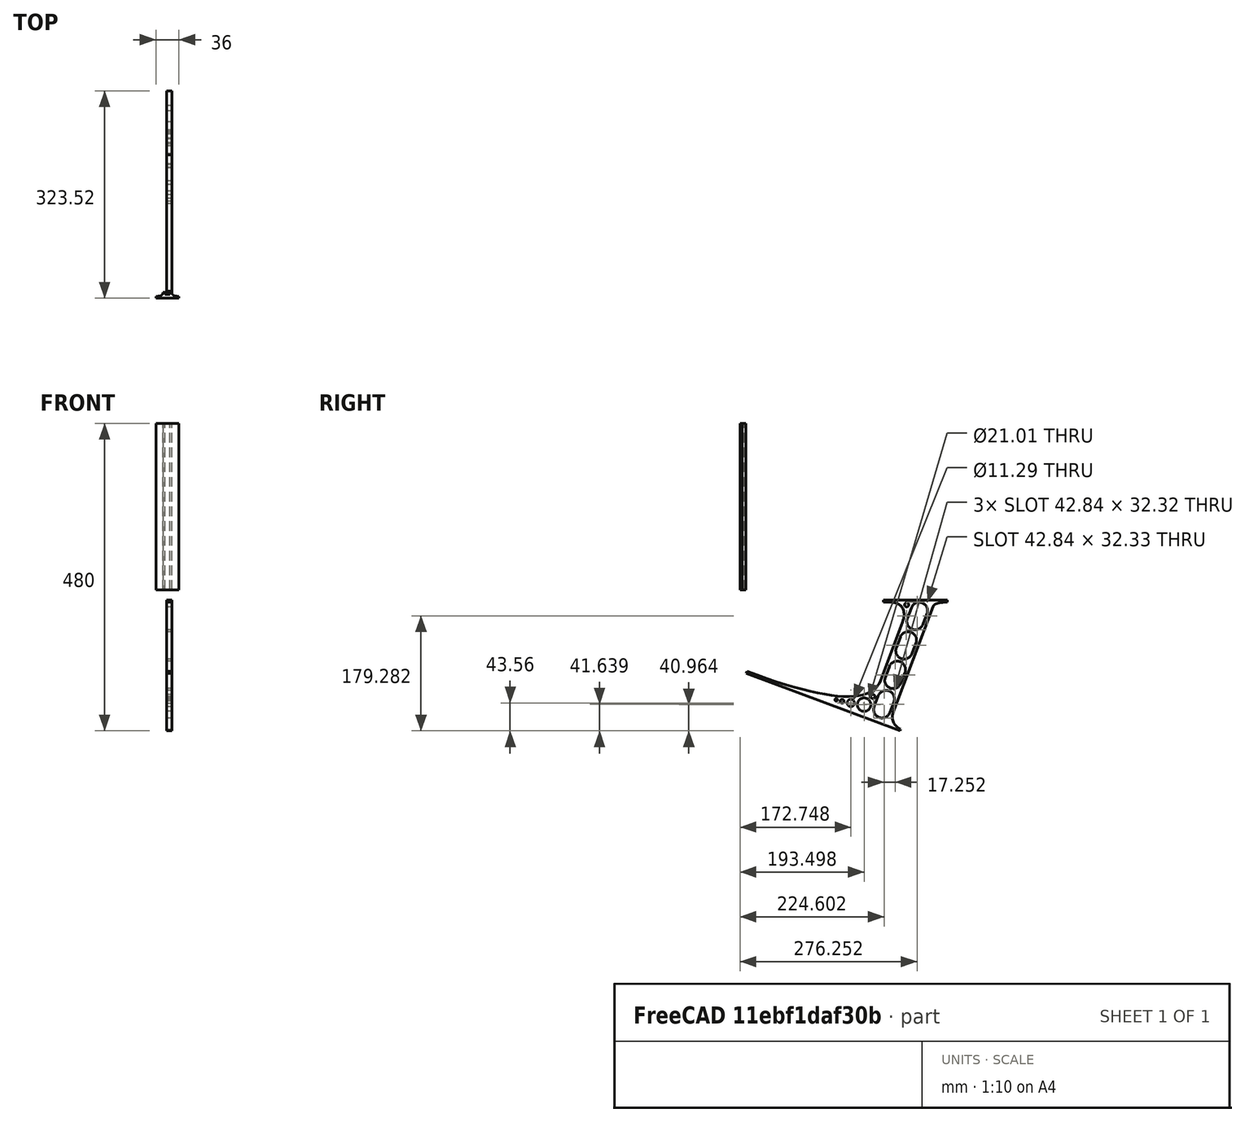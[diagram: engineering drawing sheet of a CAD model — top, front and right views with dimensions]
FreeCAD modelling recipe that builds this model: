
FCSTD DOCUMENT  (FreeCAD 0.19R0.19.2)
Label: laptopStand079
License: All rights reserved
LicenseURL: http://en.wikipedia.org/wiki/All_rights_reserved
objects: Sketcher::SketchObject×3, Part::Extrusion×3
note: 6 computed .brp shape members not serialized (recipe doc carries the construction recipe); baked Part::Feature solids carry a one-line shape summary decoded from their .brp

FEATURE [Sketcher::SketchObject] Sketch
  FullyConstrained = true
  sketch-geometry (204):
    g0: LineSegment StartX=-10.9272 StartY=-82.7794 StartZ=0 EndX=46.0728 EndY=-51.4823 EndZ=0
    g1: LineSegment StartX=366.073 StartY=-91.7794 StartZ=0 EndX=318.073 EndY=-65.424 EndZ=0
    g2: LineSegment StartX=-10.9272 StartY=77.3346 StartZ=0 EndX=-10.9272 EndY=-82.7794 EndZ=0
    g3: LineSegment StartX=375.073 StartY=-82.7794 StartZ=0 EndX=375.073 EndY=83.9235 EndZ=0
    g4: LineSegment StartX=-1.92719 StartY=-91.7794 StartZ=0 EndX=46.0728 EndY=-91.7794 EndZ=0
    g5: LineSegment StartX=318.073 StartY=124.221 StartZ=0 EndX=366.073 EndY=124.221 EndZ=0
    g6: LineSegment StartX=306.073 StartY=124.221 StartZ=0 EndX=189.124 EndY=27.0628 EndZ=0
    g7: LineSegment StartX=58.0728 StartY=-91.7794 StartZ=0 EndX=175.022 EndY=5.37834 EndZ=0
    g8: LineSegment StartX=175.022 StartY=27.0628 StartZ=0 EndX=58.0728 EndY=124.221 EndZ=0
    g9: LineSegment StartX=189.124 StartY=5.37834 StartZ=0 EndX=306.073 EndY=-91.7794 EndZ=0
    g10: LineSegment StartX=306.073 StartY=77.3346 StartZ=0 EndX=306.073 EndY=-44.8935 EndZ=0
    g11: LineSegment StartX=318.073 StartY=83.9235 StartZ=0 EndX=318.073 EndY=-51.4823 EndZ=0
    g12: LineSegment StartX=318.073 StartY=-51.4823 StartZ=0 EndX=375.073 EndY=-82.7794 EndZ=0
    g13: LineSegment StartX=318.073 StartY=-65.424 StartZ=0 EndX=318.073 EndY=-91.7794 EndZ=0
    g14: LineSegment StartX=318.073 StartY=-91.7794 StartZ=0 EndX=366.073 EndY=-91.7794 EndZ=0
    g15: LineSegment StartX=58.0728 StartY=-44.8935 StartZ=0 EndX=58.0728 EndY=77.3346 EndZ=0
    g16: LineSegment StartX=46.0728 StartY=-65.424 StartZ=0 EndX=-1.92719 EndY=-91.7794 EndZ=0
    g17: LineSegment StartX=46.0728 StartY=-65.424 StartZ=0 EndX=46.0728 EndY=-91.7794 EndZ=0
    g18: LineSegment StartX=46.0728 StartY=77.3346 StartZ=0 EndX=46.0728 EndY=-51.4823 EndZ=0
    g19: LineSegment StartX=-42.9272 StartY=136.221 StartZ=0 EndX=-42.9272 EndY=-103.779 EndZ=0
    g20: LineSegment StartX=407.073 StartY=136.221 StartZ=0 EndX=407.073 EndY=-103.779 EndZ=0
    g21: LineSegment StartX=179.022 StartY=27.0628 StartZ=0 EndX=179.022 EndY=124.221 EndZ=0
    g22: LineSegment StartX=185.124 StartY=27.0628 StartZ=0 EndX=185.124 EndY=124.221 EndZ=0
    g23: ArcOfCircle CenterX=-26.9272 CenterY=22.1087 CenterZ=0 NormalX=0 NormalY=0 NormalZ=1 AngleXU=0 Radius=8 StartAngle=1e-16 EndAngle=3.14159
    g24: ArcOfCircle CenterX=-26.9272 CenterY=-83.7794 CenterZ=0 NormalX=0 NormalY=0 NormalZ=1 AngleXU=0 Radius=8 StartAngle=3.14159 EndAngle=6.28319
    g25: LineSegment StartX=-34.9272 StartY=22.1087 StartZ=0 EndX=-34.9272 EndY=-83.7794 EndZ=0
    g26: LineSegment StartX=-18.9272 StartY=22.1087 StartZ=0 EndX=-18.9272 EndY=-83.7794 EndZ=0
    g27: LineSegment StartX=185.124 StartY=-91.7794 StartZ=0 EndX=306.073 EndY=-91.7794 EndZ=0
    g28: LineSegment StartX=179.022 StartY=-91.7794 StartZ=0 EndX=58.0728 EndY=-91.7794 EndZ=0
    g29: LineSegment StartX=306.073 StartY=124.221 StartZ=0 EndX=185.124 EndY=124.221 EndZ=0
    g30: LineSegment StartX=179.022 StartY=124.221 StartZ=0 EndX=58.0728 EndY=124.221 EndZ=0
    g31: ArcOfCircle CenterX=391.073 CenterY=22.1087 CenterZ=0 NormalX=0 NormalY=0 NormalZ=1 AngleXU=0 Radius=8 StartAngle=-4.4e-15 EndAngle=3.14159
    g32: LineSegment StartX=399.073 StartY=22.1087 StartZ=0 EndX=399.073 EndY=-83.7794 EndZ=0
    g33: LineSegment StartX=383.073 StartY=22.1087 StartZ=0 EndX=383.073 EndY=-83.7794 EndZ=0
    g34: ArcOfCircle CenterX=391.073 CenterY=-83.7794 CenterZ=0 NormalX=0 NormalY=0 NormalZ=1 AngleXU=0 Radius=8 StartAngle=3.14159 EndAngle=6.28319
    g35: Circle CenterX=175.022 CenterY=27.0628 CenterZ=0 NormalX=0 NormalY=0 NormalZ=1 AngleXU=0 Radius=1
    g36: Circle CenterX=179.022 CenterY=24.8665 CenterZ=0 NormalX=0 NormalY=0 NormalZ=1 AngleXU=0 Radius=1
    g37: Circle CenterX=179.022 CenterY=27.0628 CenterZ=0 NormalX=0 NormalY=0 NormalZ=1 AngleXU=0 Radius=1
    g38: BSplineCurve PolesCount=3 KnotsCount=2 Degree=2 IsPeriodic=0
    g39: GeomPoint X=175.022 Y=27.0628 Z=0
    g40: GeomPoint X=179.022 Y=27.0628 Z=0
    g41: Circle CenterX=189.124 CenterY=27.0628 CenterZ=0 NormalX=0 NormalY=0 NormalZ=1 AngleXU=0 Radius=1
    g42: Circle CenterX=185.124 CenterY=24.8665 CenterZ=0 NormalX=0 NormalY=0 NormalZ=1 AngleXU=0 Radius=1
    g43: Circle CenterX=185.124 CenterY=27.0628 CenterZ=0 NormalX=0 NormalY=0 NormalZ=1 AngleXU=0 Radius=1
    g44: BSplineCurve PolesCount=3 KnotsCount=2 Degree=2 IsPeriodic=0
    g45: GeomPoint X=189.124 Y=27.0628 Z=0
    g46: GeomPoint X=185.124 Y=27.0628 Z=0
    g47: Circle CenterX=175.022 CenterY=5.37834 CenterZ=0 NormalX=0 NormalY=0 NormalZ=1 AngleXU=0 Radius=1
    g48: Circle CenterX=179.022 CenterY=7.57463 CenterZ=0 NormalX=0 NormalY=0 NormalZ=1 AngleXU=0 Radius=1
    g49: Circle CenterX=179.022 CenterY=5.34704 CenterZ=0 NormalX=0 NormalY=0 NormalZ=1 AngleXU=0 Radius=1
    g50: BSplineCurve PolesCount=3 KnotsCount=2 Degree=2 IsPeriodic=0
    g51: GeomPoint X=175.022 Y=5.37834 Z=0
    g52: GeomPoint X=179.022 Y=5.34704 Z=0
    g53: Circle CenterX=189.124 CenterY=5.37834 CenterZ=0 NormalX=0 NormalY=0 NormalZ=1 AngleXU=0 Radius=1
    g54: Circle CenterX=185.124 CenterY=7.57463 CenterZ=0 NormalX=0 NormalY=0 NormalZ=1 AngleXU=0 Radius=1
    g55: Circle CenterX=185.124 CenterY=5.34704 CenterZ=0 NormalX=0 NormalY=0 NormalZ=1 AngleXU=0 Radius=1
    g56: BSplineCurve PolesCount=3 KnotsCount=2 Degree=2 IsPeriodic=0
    g57: GeomPoint X=189.124 Y=5.37834 Z=0
    g58: GeomPoint X=185.124 Y=5.34704 Z=0
    g59: LineSegment StartX=179.022 StartY=5.34704 StartZ=0 EndX=179.022 EndY=-91.7794 EndZ=0
    g60: LineSegment StartX=185.124 StartY=-91.7794 StartZ=0 EndX=185.124 EndY=5.34704 EndZ=0
    g61: Circle CenterX=165.871 CenterY=18.1458 CenterZ=0 NormalX=0 NormalY=0 NormalZ=1 AngleXU=0 Radius=1
    g62: Circle CenterX=169.377 CenterY=16.2206 CenterZ=0 NormalX=0 NormalY=0 NormalZ=1 AngleXU=0 Radius=1
    g63: Circle CenterX=165.871 CenterY=14.2954 CenterZ=0 NormalX=0 NormalY=0 NormalZ=1 AngleXU=0 Radius=1
    g64: BSplineCurve PolesCount=3 KnotsCount=2 Degree=2 IsPeriodic=0
    g65: GeomPoint X=165.871 Y=18.1458 Z=0
    g66: GeomPoint X=165.871 Y=14.2954 Z=0
    g67: Circle CenterX=198.275 CenterY=18.1458 CenterZ=0 NormalX=0 NormalY=0 NormalZ=1 AngleXU=0 Radius=1
    g68: Circle CenterX=194.768 CenterY=16.2206 CenterZ=0 NormalX=0 NormalY=0 NormalZ=1 AngleXU=0 Radius=1
    g69: Circle CenterX=198.275 CenterY=14.2954 CenterZ=0 NormalX=0 NormalY=0 NormalZ=1 AngleXU=0 Radius=1
    g70: BSplineCurve PolesCount=3 KnotsCount=2 Degree=2 IsPeriodic=0
    g71: GeomPoint X=198.275 Y=18.1458 Z=0
    g72: GeomPoint X=198.275 Y=14.2954 Z=0
    g73: LineSegment StartX=165.871 StartY=18.1458 StartZ=0 EndX=58.0728 EndY=77.3346 EndZ=0
    g74: LineSegment StartX=58.0728 StartY=-44.8935 StartZ=0 EndX=165.871 EndY=14.2954 EndZ=0
    g75: LineSegment StartX=198.275 StartY=18.1458 StartZ=0 EndX=306.073 EndY=77.3346 EndZ=0
    g76: LineSegment StartX=198.275 StartY=14.2954 StartZ=0 EndX=306.073 EndY=-44.8935 EndZ=0
    g77: LineSegment StartX=407.073 StartY=-103.779 StartZ=0 EndX=-42.9272 EndY=-103.779 EndZ=0
    g78: LineSegment StartX=407.073 StartY=136.221 StartZ=0 EndX=-42.9272 EndY=136.221 EndZ=0
    g79: LineSegment StartX=46.0728 StartY=77.3346 StartZ=0 EndX=-10.9272 EndY=77.3346 EndZ=0
    g80: LineSegment StartX=46.0728 StartY=105.865 StartZ=0 EndX=31.5028 EndY=105.865 EndZ=0
    g81: LineSegment StartX=46.0728 StartY=124.221 StartZ=0 EndX=46.0728 EndY=105.865 EndZ=0
    g82: LineSegment StartX=-1.92719 StartY=124.221 StartZ=0 EndX=31.5028 EndY=105.865 EndZ=0
    g83: LineSegment StartX=46.0728 StartY=124.221 StartZ=0 EndX=-1.92719 EndY=124.221 EndZ=0
    g84: LineSegment StartX=318.073 StartY=83.9235 StartZ=0 EndX=375.073 EndY=83.9235 EndZ=0
    g85: LineSegment StartX=318.073 StartY=105.865 StartZ=0 EndX=332.643 EndY=105.865 EndZ=0
    g86: LineSegment StartX=332.643 StartY=105.865 StartZ=0 EndX=366.073 EndY=124.221 EndZ=0
    g87: LineSegment StartX=318.073 StartY=124.221 StartZ=0 EndX=318.073 EndY=105.865 EndZ=0
    g88: Circle CenterX=125.607 CenterY=54.1951 CenterZ=0 NormalX=0 NormalY=0 NormalZ=1 AngleXU=0 Radius=1
    g89: Circle CenterX=139.632 CenterY=46.4944 CenterZ=0 NormalX=0 NormalY=0 NormalZ=1 AngleXU=0 Radius=1
    g90: Circle CenterX=127.326 CenterY=56.7187 CenterZ=0 NormalX=0 NormalY=0 NormalZ=1 AngleXU=0 Radius=1
    g91: BSplineCurve PolesCount=3 KnotsCount=2 Degree=2 IsPeriodic=0
    g92: GeomPoint X=125.607 Y=54.1951 Z=0
    g93: GeomPoint X=127.326 Y=56.7187 Z=0
    g94: Circle CenterX=236.821 CenterY=56.7187 CenterZ=0 NormalX=0 NormalY=0 NormalZ=1 AngleXU=0 Radius=1
    g95: Circle CenterX=224.513 CenterY=46.4944 CenterZ=0 NormalX=0 NormalY=0 NormalZ=1 AngleXU=0 Radius=1
    g96: Circle CenterX=238.538 CenterY=54.1951 CenterZ=0 NormalX=0 NormalY=0 NormalZ=1 AngleXU=0 Radius=1
    g97: BSplineCurve PolesCount=3 KnotsCount=2 Degree=2 IsPeriodic=0
    g98: GeomPoint X=236.821 Y=56.7187 Z=0
    g99: GeomPoint X=238.538 Y=54.1951 Z=0
    g100: Circle CenterX=238.538 CenterY=-21.7539 CenterZ=0 NormalX=0 NormalY=0 NormalZ=1 AngleXU=0 Radius=1
    g101: Circle CenterX=224.513 CenterY=-14.0532 CenterZ=0 NormalX=0 NormalY=0 NormalZ=1 AngleXU=0 Radius=1
    g102: Circle CenterX=236.821 CenterY=-24.2775 CenterZ=0 NormalX=0 NormalY=0 NormalZ=1 AngleXU=0 Radius=1
    g103: BSplineCurve PolesCount=3 KnotsCount=2 Degree=2 IsPeriodic=0
    g104: GeomPoint X=238.538 Y=-21.7539 Z=0
    g105: GeomPoint X=236.821 Y=-24.2775 Z=0
    g106: Circle CenterX=125.607 CenterY=-21.7539 CenterZ=0 NormalX=0 NormalY=0 NormalZ=1 AngleXU=0 Radius=1
    g107: Circle CenterX=139.632 CenterY=-14.0532 CenterZ=0 NormalX=0 NormalY=0 NormalZ=1 AngleXU=0 Radius=1
    g108: Circle CenterX=127.325 CenterY=-24.2775 CenterZ=0 NormalX=0 NormalY=0 NormalZ=1 AngleXU=0 Radius=1
    g109: BSplineCurve PolesCount=3 KnotsCount=2 Degree=2 IsPeriodic=0
    g110: GeomPoint X=125.607 Y=-21.7539 Z=0
    g111: GeomPoint X=127.325 Y=-24.2775 Z=0
    g112: Circle CenterX=302.996 CenterY=111.695 CenterZ=0 NormalX=0 NormalY=0 NormalZ=1 AngleXU=0 Radius=1
    g113: Circle CenterX=306.073 CenterY=114.251 CenterZ=0 NormalX=0 NormalY=0 NormalZ=1 AngleXU=0 Radius=1
    g114: Circle CenterX=306.073 CenterY=110.251 CenterZ=0 NormalX=0 NormalY=0 NormalZ=1 AngleXU=0 Radius=1
    g115: BSplineCurve PolesCount=3 KnotsCount=2 Degree=2 IsPeriodic=0
    g116: GeomPoint X=302.996 Y=111.695 Z=0
    g117: GeomPoint X=306.073 Y=110.251 Z=0
    g118: Circle CenterX=306.073 CenterY=95.2763 CenterZ=0 NormalX=0 NormalY=0 NormalZ=1 AngleXU=0 Radius=1
    g119: Circle CenterX=306.073 CenterY=91.2763 CenterZ=0 NormalX=0 NormalY=0 NormalZ=1 AngleXU=0 Radius=1
    g120: Circle CenterX=302.567 CenterY=89.3511 CenterZ=0 NormalX=0 NormalY=0 NormalZ=1 AngleXU=0 Radius=1
    g121: BSplineCurve PolesCount=3 KnotsCount=2 Degree=2 IsPeriodic=0
    g122: GeomPoint X=306.073 Y=95.2763 Z=0
    g123: GeomPoint X=302.567 Y=89.3511 Z=0
    g124: LineSegment StartX=306.073 StartY=110.251 StartZ=0 EndX=306.073 EndY=95.2763 EndZ=0
    g125: LineSegment StartX=302.996 StartY=111.695 StartZ=0 EndX=236.821 EndY=56.7187 EndZ=0
    g126: LineSegment StartX=238.538 StartY=54.1951 StartZ=0 EndX=302.567 EndY=89.3511 EndZ=0
    g127: Circle CenterX=61.1496 CenterY=111.695 CenterZ=0 NormalX=0 NormalY=0 NormalZ=1 AngleXU=0 Radius=1
    g128: Circle CenterX=58.0728 CenterY=114.251 CenterZ=0 NormalX=0 NormalY=0 NormalZ=1 AngleXU=0 Radius=1
    g129: Circle CenterX=58.0728 CenterY=110.251 CenterZ=0 NormalX=0 NormalY=0 NormalZ=1 AngleXU=0 Radius=1
    g130: BSplineCurve PolesCount=3 KnotsCount=2 Degree=2 IsPeriodic=0
    g131: GeomPoint X=61.1496 Y=111.695 Z=0
    g132: GeomPoint X=58.0728 Y=110.251 Z=0
    g133: Circle CenterX=61.5791 CenterY=89.3511 CenterZ=0 NormalX=0 NormalY=0 NormalZ=1 AngleXU=0 Radius=1
    g134: Circle CenterX=58.0728 CenterY=91.2763 CenterZ=0 NormalX=0 NormalY=0 NormalZ=1 AngleXU=0 Radius=1
    g135: Circle CenterX=58.0728 CenterY=95.2763 CenterZ=0 NormalX=0 NormalY=0 NormalZ=1 AngleXU=0 Radius=1
    g136: BSplineCurve PolesCount=3 KnotsCount=2 Degree=2 IsPeriodic=0
    g137: GeomPoint X=61.5791 Y=89.3511 Z=0
    g138: GeomPoint X=58.0728 Y=95.2763 Z=0
    g139: LineSegment StartX=58.0728 StartY=110.251 StartZ=0 EndX=58.0728 EndY=95.2763 EndZ=0
    g140: LineSegment StartX=61.1496 StartY=111.695 StartZ=0 EndX=127.326 EndY=56.7187 EndZ=0
    g141: LineSegment StartX=125.607 StartY=54.1951 StartZ=0 EndX=61.5791 EndY=89.3511 EndZ=0
    g142: Circle CenterX=61.5791 CenterY=-56.9099 CenterZ=0 NormalX=0 NormalY=0 NormalZ=1 AngleXU=0 Radius=1
    g143: Circle CenterX=58.0728 CenterY=-58.8351 CenterZ=0 NormalX=0 NormalY=0 NormalZ=1 AngleXU=0 Radius=1
    g144: Circle CenterX=58.0728 CenterY=-62.8351 CenterZ=0 NormalX=0 NormalY=0 NormalZ=1 AngleXU=0 Radius=1
    g145: BSplineCurve PolesCount=3 KnotsCount=2 Degree=2 IsPeriodic=0
    g146: GeomPoint X=61.5791 Y=-56.9099 Z=0
    g147: GeomPoint X=58.0728 Y=-62.8351 Z=0
    g148: Circle CenterX=58.0728 CenterY=-77.8102 CenterZ=0 NormalX=0 NormalY=0 NormalZ=1 AngleXU=0 Radius=1
    g149: Circle CenterX=58.0728 CenterY=-81.8102 CenterZ=0 NormalX=0 NormalY=0 NormalZ=1 AngleXU=0 Radius=1
    g150: Circle CenterX=61.1496 CenterY=-79.2541 CenterZ=0 NormalX=0 NormalY=0 NormalZ=1 AngleXU=0 Radius=1
    g151: BSplineCurve PolesCount=3 KnotsCount=2 Degree=2 IsPeriodic=0
    g152: GeomPoint X=58.0728 Y=-77.8102 Z=0
    g153: GeomPoint X=61.1496 Y=-79.2541 Z=0
    g154: LineSegment StartX=58.0728 StartY=-62.8351 StartZ=0 EndX=58.0728 EndY=-77.8102 EndZ=0
    g155: LineSegment StartX=61.1496 StartY=-79.2541 StartZ=0 EndX=127.325 EndY=-24.2775 EndZ=0
    g156: LineSegment StartX=125.607 StartY=-21.7539 StartZ=0 EndX=61.5791 EndY=-56.9099 EndZ=0
    g157: Circle CenterX=302.567 CenterY=-56.9099 CenterZ=0 NormalX=0 NormalY=0 NormalZ=1 AngleXU=0 Radius=1
    g158: Circle CenterX=306.073 CenterY=-58.8351 CenterZ=0 NormalX=0 NormalY=0 NormalZ=1 AngleXU=0 Radius=1
    g159: Circle CenterX=306.073 CenterY=-62.8351 CenterZ=0 NormalX=0 NormalY=0 NormalZ=1 AngleXU=0 Radius=1
    g160: BSplineCurve PolesCount=3 KnotsCount=2 Degree=2 IsPeriodic=0
    g161: GeomPoint X=302.567 Y=-56.9099 Z=0
    g162: GeomPoint X=306.073 Y=-62.8351 Z=0
    g163: Circle CenterX=302.996 CenterY=-79.2541 CenterZ=0 NormalX=0 NormalY=0 NormalZ=1 AngleXU=0 Radius=1
    g164: Circle CenterX=306.073 CenterY=-81.8102 CenterZ=0 NormalX=0 NormalY=0 NormalZ=1 AngleXU=0 Radius=1
    g165: Circle CenterX=306.073 CenterY=-77.8102 CenterZ=0 NormalX=0 NormalY=0 NormalZ=1 AngleXU=0 Radius=1
    g166: BSplineCurve PolesCount=3 KnotsCount=2 Degree=2 IsPeriodic=0
    g167: GeomPoint X=302.996 Y=-79.2541 Z=0
    g168: GeomPoint X=306.073 Y=-77.8102 Z=0
    g169: LineSegment StartX=306.073 StartY=-62.8351 StartZ=0 EndX=306.073 EndY=-77.8102 EndZ=0
    g170: LineSegment StartX=302.996 StartY=-79.2541 StartZ=0 EndX=236.821 EndY=-24.2775 EndZ=0
    g171: LineSegment StartX=238.538 StartY=-21.7539 StartZ=0 EndX=302.567 EndY=-56.9099 EndZ=0
    g172: LineSegment StartX=58.0728 StartY=-91.7794 StartZ=0 EndX=63.9135 EndY=-91.7794 EndZ=0
    g173: LineSegment StartX=58.0728 StartY=-91.7794 StartZ=0 EndX=61.6457 EndY=-88.8112 EndZ=0
    g174: LineSegment StartX=179.022 StartY=-91.7794 StartZ=0 EndX=171.895 EndY=-91.7794 EndZ=0
    g175: LineSegment StartX=179.022 StartY=-91.7794 StartZ=0 EndX=179.022 EndY=-85.8163 EndZ=0
    g176: LineSegment StartX=185.124 StartY=-91.7794 StartZ=0 EndX=185.124 EndY=-86.2028 EndZ=0
    g177: LineSegment StartX=185.124 StartY=-91.7794 StartZ=0 EndX=191.747 EndY=-91.7794 EndZ=0
    g178: LineSegment StartX=306.073 StartY=-91.7794 StartZ=0 EndX=298.776 EndY=-91.7794 EndZ=0
    g179: LineSegment StartX=306.073 StartY=-91.7794 StartZ=0 EndX=299.888 EndY=-86.6413 EndZ=0
    g180: Circle CenterX=61.6457 CenterY=-88.8112 CenterZ=0 NormalX=0 NormalY=0 NormalZ=1 AngleXU=0 Radius=1
    g181: Circle CenterX=58.0728 CenterY=-91.7794 CenterZ=0 NormalX=0 NormalY=0 NormalZ=1 AngleXU=0 Radius=1
    g182: Circle CenterX=63.9135 CenterY=-91.7794 CenterZ=0 NormalX=0 NormalY=0 NormalZ=1 AngleXU=0 Radius=1
    g183: BSplineCurve PolesCount=3 KnotsCount=2 Degree=2 IsPeriodic=0
    g184: GeomPoint X=61.6457 Y=-88.8112 Z=0
    g185: GeomPoint X=63.9135 Y=-91.7794 Z=0
    g186: Circle CenterX=179.022 CenterY=-85.8163 CenterZ=0 NormalX=0 NormalY=0 NormalZ=1 AngleXU=0 Radius=1
    g187: Circle CenterX=179.022 CenterY=-91.7794 CenterZ=0 NormalX=0 NormalY=0 NormalZ=1 AngleXU=0 Radius=1
    g188: Circle CenterX=171.895 CenterY=-91.7794 CenterZ=0 NormalX=0 NormalY=0 NormalZ=1 AngleXU=0 Radius=1
    g189: BSplineCurve PolesCount=3 KnotsCount=2 Degree=2 IsPeriodic=0
    g190: GeomPoint X=179.022 Y=-85.8163 Z=0
    g191: GeomPoint X=171.895 Y=-91.7794 Z=0
    g192: Circle CenterX=185.124 CenterY=-86.2028 CenterZ=0 NormalX=0 NormalY=0 NormalZ=1 AngleXU=0 Radius=1
    g193: Circle CenterX=185.124 CenterY=-91.7794 CenterZ=0 NormalX=0 NormalY=0 NormalZ=1 AngleXU=0 Radius=1
    g194: Circle CenterX=191.747 CenterY=-91.7794 CenterZ=0 NormalX=0 NormalY=0 NormalZ=1 AngleXU=0 Radius=1
    g195: BSplineCurve PolesCount=3 KnotsCount=2 Degree=2 IsPeriodic=0
    g196: GeomPoint X=185.124 Y=-86.2028 Z=0
    g197: GeomPoint X=191.747 Y=-91.7794 Z=0
    g198: Circle CenterX=299.888 CenterY=-86.6413 CenterZ=0 NormalX=0 NormalY=0 NormalZ=1 AngleXU=0 Radius=1
    g199: Circle CenterX=306.073 CenterY=-91.7794 CenterZ=0 NormalX=0 NormalY=0 NormalZ=1 AngleXU=0 Radius=1
    g200: Circle CenterX=298.776 CenterY=-91.7794 CenterZ=0 NormalX=0 NormalY=0 NormalZ=1 AngleXU=0 Radius=1
    g201: BSplineCurve PolesCount=3 KnotsCount=2 Degree=2 IsPeriodic=0
    g202: GeomPoint X=299.888 Y=-86.6413 Z=0
    g203: GeomPoint X=298.776 Y=-91.7794 Z=0
  constraints (364):
    c: Horizontal(g4)
    c: Horizontal(g5)
    c: Coincident(g11,g12)
    c: Coincident(g13,g1)
    c: Tangent(g11,g13)
    c: Coincident(g17,g16)
    c: Coincident(g0,g18)
    c: Block(g8)
    c: Block(g6)
    c: Block(g12)
    c: Block(g3)
    c: Block(g1)
    c: Block(g13)
    c: Block(g9)
    c: Block(g7)
    c: Block(g17)
    c: Block(g16)
    c: Block(g0)
    c: Block(g2)
    c: Block(g10)
    c: Block(g5)
    c: Block(g14)
    c: Block(g4)
    c: Vertical(g19)
    c: Vertical(g20)
    c: Block(g20)
    c: Block(g19)
    c: Vertical(g21)
    c: Vertical(g22)
    c: Block(g21)
    c: Block(g22)
    c: Tangent(g23,g26) = 1.5708
    c: Tangent(g23,g25) = -1.5708
    c: Tangent(g25,g24) = -1.5708
    c: Tangent(g26,g24) = 1.5708
    c: Vertical(g25)
    c: Equal(g23,g24)
    c: Block(g26)
    c: Block(g25)
    c: Coincident(g27,g9)
    c: Horizontal(g27)
    c: Coincident(g28,g7)
    c: Horizontal(g28)
    c: Coincident(g29,g6)
    c: Coincident(g29,g22)
    c: Horizontal(g29)
    c: Coincident(g30,g21)
    c: Coincident(g30,g8)
    c: Horizontal(g30)
    c: Tangent(g31,g32) = 1.5708
    c: Tangent(g32,g34) = 1.5708
    c: Equal(g31,g34)
    c: Coincident(g33,g31)
    c: Coincident(g33,g34)
    c: Block(g32)
    c: Block(g33)
    c: Coincident(g38,g8)
    c: Weight(g35) = 1
    c: Equal(g35,g36)
    c: Equal(g35,g37)
    c: Coincident(g38,g21)
    c: InternalAlignment(g35,g38)
    c: InternalAlignment(g36,g38)
    c: InternalAlignment(g37,g38)
    c: InternalAlignment(g39,g38)
    c: InternalAlignment(g40,g38)
    c: Coincident(g44,g6)
    c: Weight(g41) = 1
    c: Equal(g41,g42)
    c: Equal(g41,g43)
    c: Coincident(g44,g22)
    c: InternalAlignment(g41,g44)
    c: InternalAlignment(g42,g44)
    c: InternalAlignment(g43,g44)
    c: InternalAlignment(g45,g44)
    c: InternalAlignment(g46,g44)
    c: Block(g44)
    c: Block(g38)
    c: Coincident(g50,g7)
    c: Weight(g47) = 1
    c: Equal(g47,g48)
    c: Equal(g47,g49)
    c: InternalAlignment(g47,g50)
    c: InternalAlignment(g48,g50)
    c: InternalAlignment(g49,g50)
    c: InternalAlignment(g51,g50)
    c: InternalAlignment(g52,g50)
    c: Weight(g53) = 1
    c: Equal(g53,g54)
    c: Equal(g53,g55)
    c: InternalAlignment(g53,g56)
    c: InternalAlignment(g54,g56)
    c: InternalAlignment(g55,g56)
    c: InternalAlignment(g57,g56)
    c: InternalAlignment(g58,g56)
    c: Block(g56)
    c: Block(g50)
    c: Coincident(g59,g50)
    c: Coincident(g59,g28)
    c: Vertical(g59)
    c: Coincident(g60,g27)
    c: Coincident(g60,g56)
    c: Vertical(g60)
    c: Weight(g61) = 1
    c: Equal(g61,g62)
    c: Equal(g61,g63)
    c: InternalAlignment(g61,g64)
    c: InternalAlignment(g62,g64)
    c: InternalAlignment(g63,g64)
    c: InternalAlignment(g65,g64)
    c: InternalAlignment(g66,g64)
    c: Weight(g67) = 1
    c: Equal(g67,g68)
    c: Equal(g67,g69)
    c: InternalAlignment(g67,g70)
    c: InternalAlignment(g68,g70)
    c: InternalAlignment(g69,g70)
    c: InternalAlignment(g71,g70)
    c: InternalAlignment(g72,g70)
    c: Block(g64)
    c: Block(g70)
    c: Coincident(g73,g64)
    c: Coincident(g73,g15)
    c: Coincident(g74,g15)
    c: Coincident(g74,g64)
    c: Coincident(g75,g70)
    c: Coincident(g75,g10)
    c: Coincident(g76,g70)
    c: Coincident(g76,g10)
    c: Block(g15)
    c: Coincident(g77,g20)
    c: Coincident(g77,g19)
    c: Horizontal(g77)
    c: Distance(g77) = 450
    c: Coincident(g78,g20)
    c: Coincident(g78,g19)
    c: Horizontal(g78)
    c: Horizontal(g79)
    c: Coincident(g18,g79)
    c: Horizontal(g80)
    c: Vertical(g81)
    c: Block(g81)
    c: Block(g80)
    c: Block(g79)
    c: Distance(g81) = 18.3554
    c: Coincident(g83,g81)
    c: Coincident(g83,g82)
    c: Horizontal(g83)
    c: Block(g83)
    c: Block(g82)
    c: Coincident(g80,g82)
    c: Coincident(g2,g79)
    c: Coincident(g84,g11)
    c: Horizontal(g84)
    c: Horizontal(g85)
    c: Block(g84)
    c: Coincident(g86,g5)
    c: Coincident(g87,g5)
    c: Coincident(g87,g85)
    c: Vertical(g87)
    c: Block(g87)
    c: Coincident(g85,g86)
    c: Block(g86)
    c: Coincident(g3,g84)
    c: Weight(g88) = 1
    c: Equal(g88,g89)
    c: Equal(g88,g90)
    c: InternalAlignment(g88,g91)
    c: InternalAlignment(g89,g91)
    c: InternalAlignment(g90,g91)
    c: InternalAlignment(g92,g91)
    c: InternalAlignment(g93,g91)
    c: Block(g91)
    c: Weight(g94) = 1
    c: Equal(g94,g95)
    c: Equal(g94,g96)
    c: InternalAlignment(g94,g97)
    c: InternalAlignment(g95,g97)
    c: InternalAlignment(g96,g97)
    c: InternalAlignment(g98,g97)
    c: InternalAlignment(g99,g97)
    c: Block(g97)
    c: Weight(g100) = 1
    c: Equal(g100,g101)
    c: Equal(g100,g102)
    c: InternalAlignment(g100,g103)
    c: InternalAlignment(g101,g103)
    c: InternalAlignment(g102,g103)
    c: InternalAlignment(g104,g103)
    c: InternalAlignment(g105,g103)
    c: Block(g103)
    c: Weight(g106) = 1
    c: Equal(g106,g107)
    c: Equal(g106,g108)
    c: InternalAlignment(g106,g109)
    c: InternalAlignment(g107,g109)
    c: InternalAlignment(g108,g109)
    c: InternalAlignment(g110,g109)
    c: InternalAlignment(g111,g109)
    c: Block(g109)
    c: Weight(g112) = 1
    c: Equal(g112,g113)
    c: Equal(g112,g114)
    c: InternalAlignment(g112,g115)
    c: InternalAlignment(g113,g115)
    c: InternalAlignment(g114,g115)
    c: InternalAlignment(g116,g115)
    c: InternalAlignment(g117,g115)
    c: Weight(g118) = 1
    c: Equal(g118,g119)
    c: Equal(g118,g120)
    c: InternalAlignment(g118,g121)
    c: InternalAlignment(g119,g121)
    c: InternalAlignment(g120,g121)
    c: InternalAlignment(g122,g121)
    c: InternalAlignment(g123,g121)
    c: Block(g115)
    c: Block(g121)
    c: Coincident(g124,g115)
    c: Coincident(g124,g121)
    c: Vertical(g124)
    c: Coincident(g125,g115)
    c: Coincident(g125,g97)
    c: Coincident(g126,g97)
    c: Coincident(g126,g121)
    c: Weight(g127) = 1
    c: Equal(g127,g128)
    c: Equal(g127,g129)
    c: InternalAlignment(g127,g130)
    c: InternalAlignment(g128,g130)
    c: InternalAlignment(g129,g130)
    c: InternalAlignment(g131,g130)
    c: InternalAlignment(g132,g130)
    c: Weight(g133) = 1
    c: Equal(g133,g134)
    c: Equal(g133,g135)
    c: InternalAlignment(g133,g136)
    c: InternalAlignment(g134,g136)
    c: InternalAlignment(g135,g136)
    c: InternalAlignment(g137,g136)
    c: InternalAlignment(g138,g136)
    c: Block(g130)
    c: Block(g136)
    c: Coincident(g139,g130)
    c: Coincident(g139,g136)
    c: Vertical(g139)
    c: Coincident(g140,g130)
    c: Coincident(g140,g91)
    c: Coincident(g141,g91)
    c: Coincident(g141,g136)
    c: Weight(g142) = 1
    c: Equal(g142,g143)
    c: Equal(g142,g144)
    c: InternalAlignment(g142,g145)
    c: InternalAlignment(g143,g145)
    c: InternalAlignment(g144,g145)
    c: InternalAlignment(g146,g145)
    c: InternalAlignment(g147,g145)
    c: Weight(g148) = 1
    c: Equal(g148,g149)
    c: Equal(g148,g150)
    c: InternalAlignment(g148,g151)
    c: InternalAlignment(g149,g151)
    c: InternalAlignment(g150,g151)
    c: InternalAlignment(g152,g151)
    c: InternalAlignment(g153,g151)
    c: Block(g145)
    c: Block(g151)
    c: Coincident(g154,g145)
    c: Coincident(g154,g151)
    c: Vertical(g154)
    c: Coincident(g155,g151)
    c: Coincident(g155,g109)
    c: Coincident(g156,g109)
    c: Coincident(g156,g145)
    c: Weight(g157) = 1
    c: Equal(g157,g158)
    c: Equal(g157,g159)
    c: InternalAlignment(g157,g160)
    c: InternalAlignment(g158,g160)
    c: InternalAlignment(g159,g160)
    c: InternalAlignment(g161,g160)
    c: InternalAlignment(g162,g160)
    c: Weight(g163) = 1
    c: Equal(g163,g164)
    c: Equal(g163,g165)
    c: InternalAlignment(g163,g166)
    c: InternalAlignment(g164,g166)
    c: InternalAlignment(g165,g166)
    c: InternalAlignment(g167,g166)
    c: InternalAlignment(g168,g166)
    c: Block(g160)
    c: Block(g166)
    c: Coincident(g169,g160)
    c: Coincident(g169,g166)
    c: Vertical(g169)
    c: Coincident(g170,g166)
    c: Coincident(g170,g103)
    c: Coincident(g171,g103)
    c: Coincident(g171,g160)
    c: Horizontal(g172)
    c: Horizontal(g174)
    c: Vertical(g175)
    c: Vertical(g176)
    c: Horizontal(g177)
    c: Horizontal(g178)
    c: Parallel(g7,g173)
    c: Parallel(g9,g179)
    c: Coincident(g179,g9)
    c: Coincident(g178,g9)
    c: Coincident(g176,g27)
    c: Coincident(g177,g27)
    c: Coincident(g28,g175)
    c: Coincident(g174,g28)
    c: Coincident(g173,g7)
    c: Coincident(g172,g7)
    c: Coincident(g183,g173)
    c: Weight(g180) = 1
    c: Equal(g180,g181)
    c: Coincident(g181,g7)
    c: Equal(g180,g182)
    c: Coincident(g183,g172)
    c: InternalAlignment(g180,g183)
    c: InternalAlignment(g181,g183)
    c: InternalAlignment(g182,g183)
    c: InternalAlignment(g184,g183)
    c: InternalAlignment(g185,g183)
    c: Coincident(g189,g175)
    c: Weight(g186) = 1
    c: Equal(g186,g187)
    c: Coincident(g187,g28)
    c: Equal(g186,g188)
    c: Coincident(g189,g174)
    c: InternalAlignment(g186,g189)
    c: InternalAlignment(g187,g189)
    c: InternalAlignment(g188,g189)
    c: InternalAlignment(g190,g189)
    c: InternalAlignment(g191,g189)
    c: Coincident(g195,g176)
    c: Weight(g192) = 1
    c: Equal(g192,g193)
    c: Coincident(g193,g27)
    c: Equal(g192,g194)
    c: Coincident(g195,g177)
    c: InternalAlignment(g192,g195)
    c: InternalAlignment(g193,g195)
    c: InternalAlignment(g194,g195)
    c: InternalAlignment(g196,g195)
    c: InternalAlignment(g197,g195)
    c: Coincident(g201,g179)
    c: Weight(g198) = 1
    c: Equal(g198,g199)
    c: Coincident(g199,g9)
    c: Equal(g198,g200)
    c: Coincident(g201,g178)
    c: InternalAlignment(g198,g201)
    c: InternalAlignment(g199,g201)
    c: InternalAlignment(g200,g201)
    c: InternalAlignment(g202,g201)
    c: InternalAlignment(g203,g201)
    c: Block(g201)
    c: Block(g195)
    c: Block(g189)
    c: Block(g183)
FEATURE [Sketcher::SketchObject] Sketch001
  FullyConstrained = true
  MapMode = 4
  Placement = pos=(0,0,0) rot=(0.57735,0.57735,0.57735;2.0944rad)
  Support = -> [Sketch]
  sketch-geometry (46):
    g0: BSplineCurve PolesCount=3 KnotsCount=2 Degree=2 IsPeriodic=0
    g1: ArcOfCircle CenterX=73.1223 CenterY=-32.291 CenterZ=0 NormalX=0 NormalY=0 NormalZ=1 AngleXU=0 Radius=13 StartAngle=5.92268 EndAngle=9.06428
    g2: ArcOfCircle CenterX=66.7816 CenterY=-49.1439 CenterZ=0 NormalX=0 NormalY=0 NormalZ=1 AngleXU=0 Radius=13 StartAngle=2.78068 EndAngle=5.92131
    g3: ArcOfCircle CenterX=55.9263 CenterY=-78.1807 CenterZ=0 NormalX=0 NormalY=0 NormalZ=1 AngleXU=0 Radius=13 StartAngle=5.92268 EndAngle=9.06428
    g4: ArcOfCircle CenterX=49.5884 CenterY=-95.0342 CenterZ=0 NormalX=0 NormalY=0 NormalZ=1 AngleXU=0 Radius=13 StartAngle=2.78068 EndAngle=5.92131
    g5: ArcOfCircle CenterX=38.7206 CenterY=-124.067 CenterZ=0 NormalX=0 NormalY=0 NormalZ=1 AngleXU=0 Radius=13 StartAngle=5.92268 EndAngle=9.06428
    g6: ArcOfCircle CenterX=32.3875 CenterY=-140.92 CenterZ=0 NormalX=0 NormalY=0 NormalZ=1 AngleXU=0 Radius=13 StartAngle=2.78068 EndAngle=5.92131
    g7: ArcOfCircle CenterX=21.4715 CenterY=-169.934 CenterZ=0 NormalX=0 NormalY=0 NormalZ=1 AngleXU=0 Radius=13 StartAngle=5.92268 EndAngle=9.06428
    g8: ArcOfCircle CenterX=15.1336 CenterY=-186.787 CenterZ=0 NormalX=0 NormalY=0 NormalZ=1 AngleXU=0 Radius=13 StartAngle=2.78068 EndAngle=5.92131
    g9-g12: Circle x4 (B-spline internal-alignment scaffolding for g13; pole/knot coordinates omitted)
    g13: BSplineCurve PolesCount=4 KnotsCount=2 Degree=3 IsPeriodic=0
    g14: GeomPoint X=28.8094 Y=-19.0875 Z=0
    g15: GeomPoint X=47.0443 Y=-50.4712 Z=0
    g16: Circle CenterX=53.5586 CenterY=-23.2695 CenterZ=0 NormalX=0 NormalY=0 NormalZ=1 AngleXU=0 Radius=3.24518
    g17: Circle CenterX=-195.441 CenterY=-127.082 CenterZ=0 NormalX=0 NormalY=0 NormalZ=1 AngleXU=0 Radius=1
    g18: Circle CenterX=-8.24091 CenterY=-197.481 CenterZ=0 NormalX=0 NormalY=0 NormalZ=1 AngleXU=0 Radius=1
    g19: Circle CenterX=12.8789 CenterY=-141.321 CenterZ=0 NormalX=0 NormalY=0 NormalZ=1 AngleXU=0 Radius=1
    g20: BSplineCurve PolesCount=3 KnotsCount=2 Degree=2 IsPeriodic=0
    g21: GeomPoint X=-195.441 Y=-127.082 Z=0
    g22: GeomPoint X=12.8789 Y=-141.321 Z=0
    g23: Circle CenterX=-12.8016 CenterY=-179.036 CenterZ=0 NormalX=0 NormalY=0 NormalZ=1 AngleXU=0 Radius=10.5072
    g24: Circle CenterX=0.933922 CenterY=-166.43 CenterZ=0 NormalX=0 NormalY=0 NormalZ=1 AngleXU=0 Radius=3.26661
    g25: Circle CenterX=-33.5518 CenterY=-176.44 CenterZ=0 NormalX=0 NormalY=0 NormalZ=1 AngleXU=0 Radius=5.64388
    g26: Circle CenterX=-47.2366 CenterY=-173.859 CenterZ=0 NormalX=0 NormalY=0 NormalZ=1 AngleXU=0 Radius=3.01653
    g27: Circle CenterX=-56.2595 CenterY=-171.456 CenterZ=0 NormalX=0 NormalY=0 NormalZ=1 AngleXU=0 Radius=2.12826
    g28: ArcOfCircle CenterX=51.2151 CenterY=-198.473 CenterZ=0 NormalX=0 NormalY=0 NormalZ=1 AngleXU=0 Radius=20 StartAngle=2.78189 EndAngle=4.35269
    g29: LineSegment StartX=32.4951 StartY=-191.433 StartZ=0 EndX=94.6578 EndY=-26.1352 EndZ=0
    g30: LineSegment StartX=43.1192 StartY=-220.001 StartZ=0 EndX=-196.497 EndY=-129.89 EndZ=0
    g31: LineSegment StartX=43.1192 StartY=-220.001 StartZ=0 EndX=44.1752 EndY=-217.193 EndZ=0
    g32: LineSegment StartX=117.223 StartY=-19.0875 StartZ=0 EndX=117.223 EndY=-16.0875 EndZ=0
    g33: LineSegment StartX=117.223 StartY=-16.0875 StartZ=0 EndX=17.2232 EndY=-16.0875 EndZ=0
    g34: LineSegment StartX=17.2232 StartY=-16.0875 StartZ=0 EndX=17.2232 EndY=-19.0875 EndZ=0
    g35: LineSegment StartX=28.8094 StartY=-19.0875 StartZ=0 EndX=17.2232 EndY=-19.0875 EndZ=0
    g36: LineSegment StartX=47.0443 StartY=-50.4712 StartZ=0 EndX=12.8789 EndY=-141.321 EndZ=0
    g37: LineSegment StartX=-195.441 StartY=-127.082 StartZ=0 EndX=-196.497 EndY=-129.89 EndZ=0
    g38: LineSegment StartX=85.2866 StartY=-36.8766 StartZ=0 EndX=78.9396 EndY=-53.7463 EndZ=0
    g39: LineSegment StartX=60.9579 StartY=-27.7053 StartZ=0 EndX=54.6191 EndY=-44.5532 EndZ=0
    g40: LineSegment StartX=68.0907 StartY=-82.7664 StartZ=0 EndX=61.7465 EndY=-99.6365 EndZ=0
    g41: LineSegment StartX=43.7619 StartY=-73.595 StartZ=0 EndX=37.426 EndY=-90.4435 EndZ=0
    g42: LineSegment StartX=50.885 StartY=-128.652 StartZ=0 EndX=44.5456 EndY=-145.522 EndZ=0
    g43: LineSegment StartX=26.5562 StartY=-119.481 StartZ=0 EndX=20.2251 EndY=-136.329 EndZ=0
    g44: LineSegment StartX=9.3071 StartY=-165.349 StartZ=0 EndX=2.97115 EndY=-182.197 EndZ=0
    g45: LineSegment StartX=33.6358 StartY=-174.52 StartZ=0 EndX=27.2917 EndY=-191.39 EndZ=0
  constraints (71):
    c: Block(g0)
    c: Block(g1)
    c: Block(g2)
    c: Block(g4)
    c: Block(g3)
    c: Block(g6)
    c: Block(g5)
    c: Block(g8)
    c: Block(g7)
    c: Weight(g9) = 1
    c: Equal(g9,g10)
    c: Equal(g9,g11)
    c: Equal(g9,g12)
    c: InternalAlignment(g9-g12 -> g13) x4
    c: InternalAlignment(g14,g13)
    c: InternalAlignment(g15,g13)
    c: Block(g16)
    c: Weight(g17) = 1
    c: Equal(g17,g18)
    c: Equal(g17,g19)
    c: InternalAlignment(g17,g20)
    c: InternalAlignment(g18,g20)
    c: InternalAlignment(g19,g20)
    c: InternalAlignment(g21,g20)
    c: InternalAlignment(g22,g20)
    c: Block(g20)
    c: Block(g23)
    c: Block(g24)
    c: Block(g25)
    c: Block(g26)
    c: Block(g27)
    c: Block(g28)
    c: Coincident(g29,g28)
    c: Coincident(g29,g0)
    c: Block(g13)
    c: Coincident(g31,g30)
    c: Coincident(g31,g28)
    c: Block(g31)
    c: Coincident(g32,g0)
    c: Vertical(g32)
    c: Coincident(g33,g32)
    c: Horizontal(g33)
    c: Coincident(g34,g33)
    c: Vertical(g34)
    c: Block(g33)
    c: Coincident(g35,g13)
    c: Coincident(g35,g34)
    c: Horizontal(g35)
    c: Coincident(g36,g13)
    c: Coincident(g36,g20)
    c: Coincident(g37,g20)
    c: Coincident(g37,g30)
    c: Block(g30)
    c: Coincident(g38,g1)
    c: Coincident(g38,g2)
    c: Coincident(g39,g1)
    c: Coincident(g39,g2)
    c: Coincident(g40,g3)
    c: Coincident(g40,g4)
    c: Coincident(g41,g3)
    c: Coincident(g41,g4)
    c: Coincident(g42,g5)
    c: Coincident(g42,g6)
    c: Coincident(g43,g5)
    c: Coincident(g43,g6)
    c: Coincident(g44,g7)
    c: Coincident(g44,g8)
    c: Coincident(g45,g7)
    c: Coincident(g45,g8)
    c: Distance(g30) = 256
    c: Distance(g33) = 100
FEATURE [Part::Extrusion] Extrude002
  Base = -> Sketch001
  Dir = (1,0,0)
  DirMode = 2
  FaceMakerClass = Part::FaceMakerBullseye
  LengthFwd = 8
  LengthRev = 0
  Solid = true
  Symmetric = false
FEATURE [Sketcher::SketchObject] Sketch002
  FullyConstrained = true
  sketch-geometry (20):
    g0: LineSegment StartX=-2.77179 StartY=-200.304 StartZ=0 EndX=5.22821 EndY=-200.304 EndZ=0
    g1: LineSegment StartX=5.22821 StartY=-200.304 StartZ=0 EndX=5.22821 EndY=-197.304 EndZ=0
    g2: LineSegment StartX=-2.77179 StartY=-200.304 StartZ=0 EndX=-2.77179 EndY=-197.304 EndZ=0
    g3: LineSegment StartX=5.22821 StartY=-197.304 StartZ=0 EndX=8.22821 EndY=-197.304 EndZ=0
    g4: LineSegment StartX=-2.77179 StartY=-197.304 StartZ=0 EndX=-5.77179 EndY=-197.304 EndZ=0
    g5: LineSegment StartX=19.2282 StartY=-203.304 StartZ=0 EndX=19.2282 EndY=-206.304 EndZ=0
    g6: LineSegment StartX=-16.7718 StartY=-203.304 StartZ=0 EndX=-16.7718 EndY=-206.304 EndZ=0
    g7: LineSegment StartX=-16.7718 StartY=-206.304 StartZ=0 EndX=19.2282 EndY=-206.304 EndZ=0
    g8: Circle CenterX=-16.7718 CenterY=-203.304 CenterZ=0 NormalX=0 NormalY=0 NormalZ=1 AngleXU=0 Radius=1
    g9: Circle CenterX=-5.77179 CenterY=-203.304 CenterZ=0 NormalX=0 NormalY=0 NormalZ=1 AngleXU=0 Radius=1
    g10: Circle CenterX=-5.77179 CenterY=-197.304 CenterZ=0 NormalX=0 NormalY=0 NormalZ=1 AngleXU=0 Radius=1
    g11: BSplineCurve PolesCount=3 KnotsCount=2 Degree=2 IsPeriodic=0
    g12: GeomPoint X=-16.7718 Y=-203.304 Z=0
    g13: GeomPoint X=-5.77179 Y=-197.304 Z=0
    g14: Circle CenterX=19.2282 CenterY=-203.304 CenterZ=0 NormalX=0 NormalY=0 NormalZ=1 AngleXU=0 Radius=1
    g15: Circle CenterX=8.22821 CenterY=-203.304 CenterZ=0 NormalX=0 NormalY=0 NormalZ=1 AngleXU=0 Radius=1
    g16: Circle CenterX=8.22821 CenterY=-197.304 CenterZ=0 NormalX=0 NormalY=0 NormalZ=1 AngleXU=0 Radius=1
    g17: BSplineCurve PolesCount=3 KnotsCount=2 Degree=2 IsPeriodic=0
    g18: GeomPoint X=19.2282 Y=-203.304 Z=0
    g19: GeomPoint X=8.22821 Y=-197.304 Z=0
  constraints (41):
    c: Horizontal(g0)
    c: Distance(g0) = 8
    c: Coincident(g1,g0)
    c: Vertical(g1)
    c: Distance(g1) = 3
    c: Coincident(g2,g0)
    c: Vertical(g2)
    c: Distance(g2) = 3
    c: Coincident(g3,g1)
    c: Horizontal(g3)
    c: Distance(g3) = 3
    c: Coincident(g4,g2)
    c: Horizontal(g4)
    c: Distance(g4) = 3
    c: Vertical(g5)
    c: Vertical(g6)
    c: Coincident(g7,g6)
    c: Coincident(g7,g5)
    c: Weight(g8) = 1
    c: Equal(g8,g9)
    c: Equal(g8,g10)
    c: Coincident(g11,g4)
    c: InternalAlignment(g8,g11)
    c: InternalAlignment(g9,g11)
    c: InternalAlignment(g10,g11)
    c: InternalAlignment(g12,g11)
    c: InternalAlignment(g13,g11)
    c: Coincident(g17,g5)
    c: Weight(g14) = 1
    c: Equal(g14,g15)
    c: Equal(g14,g16)
    c: Coincident(g17,g3)
    c: InternalAlignment(g14,g17)
    c: InternalAlignment(g15,g17)
    c: InternalAlignment(g16,g17)
    c: InternalAlignment(g18,g17)
    c: InternalAlignment(g19,g17)
    c: Block(g7)
    c: Block(g17)
    c: Block(g11)
    c: Block(g6)
FEATURE [Part::Extrusion] Extrude003
  Base = -> Sketch002
  Dir = (0,0,1)
  DirMode = 2
  FaceMakerClass = Part::FaceMakerBullseye
  LengthFwd = 260
  LengthRev = 0
  Solid = true
  Symmetric = false
FEATURE [Part::Extrusion] Extrude
  Base = -> Sketch
  Dir = (0,0,1)
  DirMode = 2
  FaceMakerClass = Part::FaceMakerBullseye
  LengthFwd = 14
  LengthRev = 0
  Solid = true
  Symmetric = false
